# Revit family: Yuno_020118
name_source: partatom
category: Furniture
revit_build: Autodesk Revit 2016 (Build: 20150714_1515(x64)
units: mm (PartAtom-declared; Revit-internal decimal feet)

## family parameters
Always vertical = Yes
Cut with Voids When Loaded = No
OmniClass Number = 23.40.20.00
OmniClass Title = General Furniture and Specialties
Room Calculation Point = No
Shared = No
Work Plane-Based = No

## types (20) — shared parameters
Manufacturer = Bernhardt Design
Model = Yuno
Module Offset = 0' - 3 3/8"
URL = http://bernhardtdesign.com

## per-type parameters (varying)
| type | Beam Width | Double Power/USB Module | Frame Inside Width | Legs Outside Width | Single Power Module | Top Depth | Top Width | Type Depth | Type Power | Type Width |
| Yuno TT1 | 2' - 0 3/8" | No | 2' - 1 1/4" | 2' - 5 3/4" | No | 2' - 0" | 4' - 7" | 1 | 0 | 1 |
| Yuno TT2 | 2' - 4 3/8" | No | 2' - 5 1/4" | 2' - 9 3/4" | No | 2' - 0" | 5' - 3" | 1 | 0 | 2 |
| Yuno TT3 | 2' - 0 3/8" | No | 2' - 1 1/4" | 2' - 5 3/4" | No | 2' - 6" | 4' - 7" | 2 | 0 | 1 |
| Yuno TT4 | 2' - 4 3/8" | No | 2' - 5 1/4" | 2' - 9 3/4" | No | 2' - 6" | 5' - 3" | 2 | 0 | 2 |
| Yuno AT1 | 2' - 0 3/8" | No | 2' - 1 1/4" | 2' - 5 3/4" | Yes | 2' - 0" | 4' - 7" | 1 | 1 | 1 |
| Yuno AT2 | 2' - 4 3/8" | No | 2' - 5 1/4" | 2' - 9 3/4" | Yes | 2' - 0" | 5' - 3" | 1 | 1 | 2 |
| Yuno AT3 | 2' - 0 3/8" | No | 2' - 1 1/4" | 2' - 5 3/4" | Yes | 2' - 6" | 4' - 7" | 2 | 1 | 1 |
| Yuno AT4 | 2' - 4 3/8" | No | 2' - 5 1/4" | 2' - 9 3/4" | Yes | 2' - 6" | 5' - 3" | 2 | 1 | 2 |
| Yuno BT1 | 2' - 0 3/8" | No | 2' - 1 1/4" | 2' - 5 3/4" | Yes | 2' - 0" | 4' - 7" | 1 | 1 | 1 |
| Yuno BT2 | 2' - 4 3/8" | No | 2' - 5 1/4" | 2' - 9 3/4" | Yes | 2' - 0" | 5' - 3" | 1 | 1 | 2 |
| Yuno BT3 | 2' - 0 3/8" | No | 2' - 1 1/4" | 2' - 5 3/4" | Yes | 2' - 6" | 4' - 7" | 2 | 1 | 1 |
| Yuno BT4 | 2' - 4 3/8" | No | 2' - 5 1/4" | 2' - 9 3/4" | Yes | 2' - 6" | 5' - 3" | 2 | 1 | 2 |
| Yuno CT1 | 2' - 0 3/8" | Yes | 2' - 1 1/4" | 2' - 5 3/4" | No | 2' - 0" | 4' - 7" | 1 | 2 | 1 |
| Yuno CT2 | 2' - 4 3/8" | Yes | 2' - 5 1/4" | 2' - 9 3/4" | No | 2' - 0" | 5' - 3" | 1 | 2 | 2 |
| Yuno CT3 | 2' - 0 3/8" | Yes | 2' - 1 1/4" | 2' - 5 3/4" | No | 2' - 6" | 4' - 7" | 2 | 2 | 1 |
| Yuno CT4 | 2' - 4 3/8" | Yes | 2' - 5 1/4" | 2' - 9 3/4" | No | 2' - 6" | 5' - 3" | 2 | 2 | 2 |
| Yuno DT1 | 2' - 0 3/8" | Yes | 2' - 1 1/4" | 2' - 5 3/4" | No | 2' - 0" | 4' - 7" | 1 | 2 | 1 |
| Yuno DT2 | 2' - 4 3/8" | Yes | 2' - 5 1/4" | 2' - 9 3/4" | No | 2' - 0" | 5' - 3" | 1 | 2 | 2 |
| Yuno DT3 | 2' - 0 3/8" | Yes | 2' - 1 1/4" | 2' - 5 3/4" | No | 2' - 6" | 4' - 7" | 2 | 2 | 1 |
| Yuno DT4 | 2' - 4 3/8" | Yes | 2' - 5 1/4" | 2' - 9 3/4" | No | 2' - 6" | 5' - 3" | 2 | 2 | 2 |

note: column(s) folded — value = type name in every type: SKU

## geometry (parser evidence)
native form markers: Sweep x1
no freeform markers — native parametric forms only
